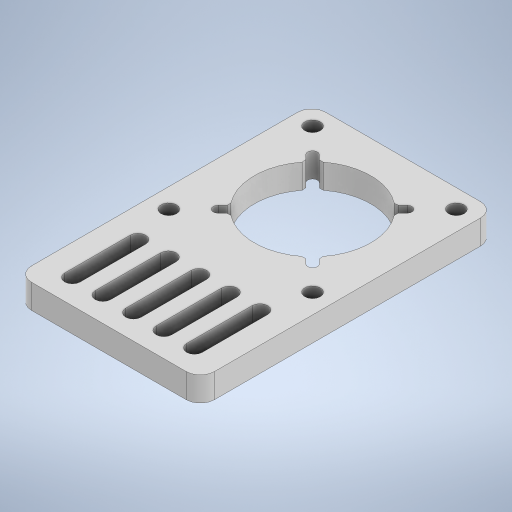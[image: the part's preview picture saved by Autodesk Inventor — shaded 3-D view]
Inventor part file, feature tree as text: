
AUTODESK INVENTOR PART (.ipt)
format: ipt  version: 2023.2 (Build 272271000, 271)  size: 393,216 bytes
history: native  units: mm
features: other x1, extrude x1, sketch x1, projected_geometry x1, chamfer x1
ambient origin geometry x8: Origin, YZ Plane, XZ Plane, XY Plane, X Axis, Y Axis, Z Axis, Center Point
bodies: Solid1 (feature_tree)
feature tree (5):
  other  "NEMA23-Motor-Mounting-Plate.step"
  extrude  "Extrusion1"  [1 undecoded]
  sketch  "Sketch1"  dims[d0=5.0mm d1=0.0mm]
  projected_geometry  "Projected Loop1"
  chamfer  "Chamfer1"  [1 undecoded]
note: 2 required parameter values undecoded (feature->parameter linkage not recoverable at this tier; creation-order binding heuristic only, values carry confidence <= 0.55)
